# Revit family: Rouge_OXXO_Standard
name_source: partatom
category: Doors
revit_build: Autodesk Revit 2014 (Build: 20130308_1515(x64)
units: mm (PartAtom-declared; Revit-internal decimal feet)

## types (10) — shared parameters
Centered In Wall = Yes
Custom Door Height = 2090 mm  [stored 6.85696 ft]
Custom Sash Width Side = 800 mm
Description = Sliding door, OXXO
Equal Sash Width = Yes
Frame Thickness = 64 mm
Height = 2090 mm  [stored 6.85696 ft]
Limit Door Height Max = 2141 mm
Limit Door Height Min = 341 mm
Limit Door Width Min = 1183 mm
Limit Sash Height Max = 2100 mm
Limit Sash Height Min = 300 mm  [stored 0.984252 ft]
Limit Sash Width Max = 1500 mm
Limit Sash Width Min = 300 mm  [stored 0.984252 ft]
Manufacturer = Crealco
Model = Rouge
Sash Frame Seal = 4 mm  [stored 0.0131234 ft]
Sash Frame Side Gap = 4 mm  [stored 0.0131234 ft]
Sash Frame Top Gap = 10 mm  [stored 0.0328084 ft]
Sash Height = 2049 mm
Sash Sliding Frame Seal = 5 mm  [stored 0.0164042 ft]
URL = http://www.crealco.co.za
Wall Closure = By host
zero-valued in all types: Custom Frame Offset From Exterior, Default Sill Height

## per-type parameters (varying)
| type | Area Middle Sash Glazing | Area Side Sash Glazing | Custom Door Width | Custom Windload | Interlock Configuration Door | Interlock Configuration Exterior | Interlock Configuration Interior | Intruderprufe LowE SHGC Value | Intruderprufe LowE U Value | Intruderprufe SHGC Value | Intruderprufe U Value | Limit Door Width Max | Limit Sash Width Side Max | Limit Sash Width Side Min | Max Pane Area | Meeting Stile Configuration | Sash Width Middle | Sash Width Sides | Toughened Safety SHGC Value | Toughened Safety U Value | Width | Windload Design |
| Rouge-3021OXXO-1000Pa | 1.32 m² | 1.42 m² | 2990 mm | 1000 mm  [stored 3.28084 ft] | 2 mm  [stored 0.00656168 ft] | 1 mm  [stored 0.00328084 ft] | 2 mm  [stored 0.00656168 ft] | 0.636 | 4.25 | 0.726 | 5.78 | 5990 mm  [stored 19.6522 ft] | 1203 mm | 300 mm  [stored 0.984252 ft] | 1.42 m² | 1 mm  [stored 0.00328084 ft] | 752 mm | 752 mm | 0.758 | 5.86 | 2990 mm | 1000 mm  [stored 3.28084 ft] |
| Rouge-3021OXXO-1500Pa | 1.32 m² | 1.42 m² | 2990 mm | 1500 mm | 4 mm  [stored 0.0131234 ft] | 2 mm  [stored 0.00656168 ft] | 2 mm  [stored 0.00656168 ft] | 0.636 | 4.25 | 0.726 | 5.78 | 3990 mm | 1203 mm | 300 mm  [stored 0.984252 ft] | 1.42 m² | 2 mm  [stored 0.00656168 ft] | 752 mm | 752 mm | 0.758 | 5.86 | 2990 mm | 1500 mm |
| Rouge-3621OXXO-1000Pa | 1.62 m² | 1.71 m² | 3590 mm | 1000 mm  [stored 3.28084 ft] | 2 mm  [stored 0.00656168 ft] | 1 mm  [stored 0.00328084 ft] | 2 mm  [stored 0.00656168 ft] | 0.644 | 4.16 | 0.735 | 5.76 | 5990 mm  [stored 19.6522 ft] | 1500 mm | 303 mm | 1.71 m² | 1 mm  [stored 0.00328084 ft] | 902 mm | 902 mm | 0.767 | 5.84 | 3590 mm | 1000 mm  [stored 3.28084 ft] |
| Rouge-3621OXXO-1500Pa | 1.62 m² | 1.71 m² | 3590 mm | 1500 mm | 3 mm  [stored 0.00984252 ft] | 1 mm  [stored 0.00328084 ft] | 3 mm  [stored 0.00984252 ft] | 0.644 | 4.16 | 0.735 | 5.76 | 3990 mm | 1500 mm | 303 mm | 1.71 m² | 2 mm  [stored 0.00656168 ft] | 902 mm | 902 mm | 0.767 | 5.847 | 3590 mm | 1500 mm |
| Rouge-4021OXXO-1000Pa | 1.82 m² | 1.91 m² | 3990 mm | 1000 mm  [stored 3.28084 ft] | 4 mm  [stored 0.0131234 ft] | 2 mm  [stored 0.00656168 ft] | 2 mm  [stored 0.00656168 ft] | 0.648 | 4.11 | 0.74 | 5.75 | 5990 mm  [stored 19.6522 ft] | 1500 mm | 503 mm | 1.91 m² | 1 mm  [stored 0.00328084 ft] | 1002 mm | 1002 mm | 0.722 | 5.83 | 3990 mm | 1000 mm  [stored 3.28084 ft] |
| Rouge-4021OXXO-1500Pa | 1.82 m² | 1.91 m² | 3990 mm | 1500 mm | 3 mm  [stored 0.00984252 ft] | 1 mm  [stored 0.00328084 ft] | 3 mm  [stored 0.00984252 ft] | 0.648 | 4.11 | 0.74 | 5.75 | 3990 mm | 1500 mm | 503 mm | 1.91 m² | 2 mm  [stored 0.00656168 ft] | 1002 mm | 1002 mm | 0.772 | 5.83 | 3990 mm | 1500 mm |
| Rouge-4221OXXO-1000Pa | 1.91 m² | 2.01 m² | 4190 mm | 1000 mm  [stored 3.28084 ft] | 4 mm  [stored 0.0131234 ft] | 2 mm  [stored 0.00656168 ft] | 2 mm  [stored 0.00656168 ft] | 0.65 | 4.09 | 0.742 | 5.75 | 5990 mm  [stored 19.6522 ft] | 1500 mm | 603 mm | 2.01 m² | 1 mm  [stored 0.00328084 ft] | 1052 mm | 1052 mm | 0.774 | 5.82 | 4190 mm | 1000 mm  [stored 3.28084 ft] |
| Rouge-4821OXXO-1000Pa | 2.21 m² | 2.3 m² | 4790 mm | 1000 mm  [stored 3.28084 ft] | 4 mm  [stored 0.0131234 ft] | 2 mm  [stored 0.00656168 ft] | 2 mm  [stored 0.00656168 ft] | 0.654 | 4.04 | 0.747 | 5.73 | 5990 mm  [stored 19.6522 ft] | 1500 mm | 903 mm | 2.3 m² | 2 mm  [stored 0.00656168 ft] | 1202 mm | 1202 mm | 0.779 | 5.81 | 4790 mm | 1000 mm  [stored 3.28084 ft] |
| Rouge-5421OXXO-1000Pa | 2.5 m² | 2.6 m² | 5390 mm | 1000 mm  [stored 3.28084 ft] | 3 mm  [stored 0.00984252 ft] | 1 mm  [stored 0.00328084 ft] | 3 mm  [stored 0.00984252 ft] | 0.657 | 4 | 0.751 | 5.72 | 5990 mm  [stored 19.6522 ft] | 1500 mm | 1203 mm | 2.6 m² | 2 mm  [stored 0.00656168 ft] | 1352 mm | 1352 mm | 0.784 | 5.8 | 5390 mm | 1000 mm  [stored 3.28084 ft] |
| Rouge-6021OXXO-1000Pa | 2.8 m² | 2.89 m² | 5990 mm  [stored 19.6522 ft] | 1000 mm  [stored 3.28084 ft] | 3 mm  [stored 0.00984252 ft] | 1 mm  [stored 0.00328084 ft] | 3 mm  [stored 0.00984252 ft] | 0.66 | 4 | 0.754 | 5.75 | 5990 mm  [stored 19.6522 ft] | 1500 mm | 1503 mm | 2.89 m² | 2 mm  [stored 0.00656168 ft] | 1502 mm | 1502 mm | 0.787 | 5.83 | 5990 mm  [stored 19.6522 ft] | 1000 mm  [stored 3.28084 ft] |

note: [stored X ft] marks values corroborated as IEEE doubles in the binary element streams (Revit-internal decimal feet)

## geometry (parser evidence)
native form markers: Sweep x48
no freeform markers — native parametric forms only
